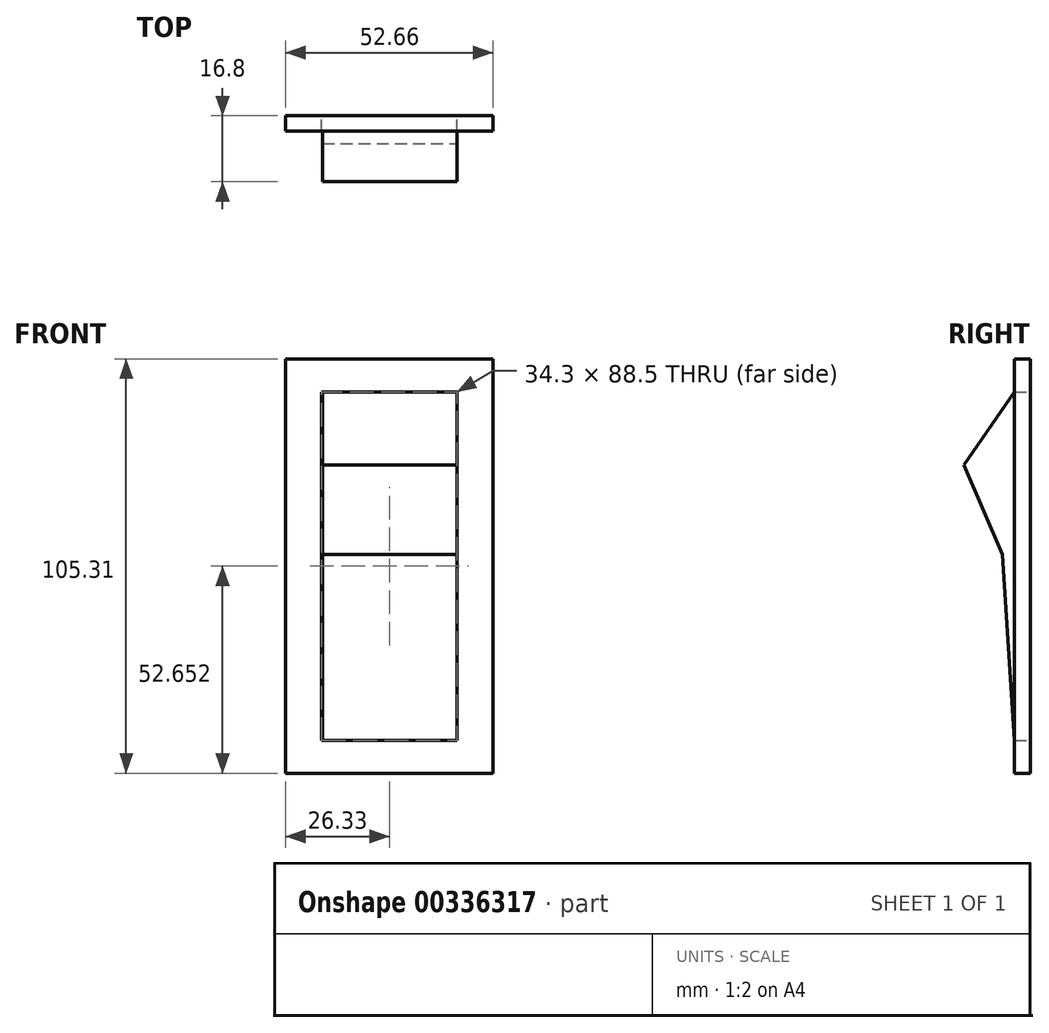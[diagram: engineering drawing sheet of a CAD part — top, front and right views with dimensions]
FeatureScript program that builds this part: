
annotation { "Feature Type Name" : "Feature", "Feature Type Description" : "" }
export const myFeature = defineFeature(function(context is Context, id is Id, definition is map)
    precondition{}
    {
        {
            var Q0;
            Q0=qCreatedBy(makeId("Front.planeOp"),FACE);
            var sketch = newSketch(context, id + "F0", { "sketchPlane" : qUnion([Q0])});
            skLineSegment(sketch, "E0.bottom", {"start": v(-29.07, 12.82) * mm, "end": v(-81.73, 12.82) * mm});
            skLineSegment(sketch, "E0.top", {"start": v(-29.07, 118.13) * mm, "end": v(-81.73, 118.13) * mm});
            skLineSegment(sketch, "E0.left", {"start": v(-29.07, 12.82) * mm, "end": v(-29.07, 118.13) * mm});
            skLineSegment(sketch, "E0.right", {"start": v(-81.73, 12.82) * mm, "end": v(-81.73, 118.13) * mm});
            skPoint(sketch, "E0.middle", {"position": v(-55.4, 65.47) * mm});
            skLineSegment(sketch, "E1.bottom", {"start": v(-72.55, 109.72) * mm, "end": v(-38.25, 109.72) * mm});
            skLineSegment(sketch, "E1.top", {"start": v(-72.55, 21.22) * mm, "end": v(-38.25, 21.22) * mm});
            skLineSegment(sketch, "E1.left", {"start": v(-72.55, 109.72) * mm, "end": v(-72.55, 21.22) * mm});
            skLineSegment(sketch, "E1.right", {"start": v(-38.25, 109.72) * mm, "end": v(-38.25, 21.22) * mm});
            skSolve(sketch);
        }
        {
            var Q0;
            Q0=makeQuery(id+"F0.imprint","IMPRINT",FACE,{"disambiguationData":[TD([[makeQuery(id+"F0.imprint","IMPRINT",EDGE,{"derivedFrom":sQuery(id+"F0.wireOp",EDGE,"E0.bottom")}),-1.0]])]});
            extrude(context, id + "F1", {"entities" : qUnion([Q0]), "depth" : 4 * mm});
        }
        {
            var Q0;
            Q0=makeQuery(id+"F1.opExtrude","SWEPT_FACE",FACE,{"disambiguationData":[OSD([sQuery(id+"F0.wireOp",EDGE,"E1.right")])]});
            var sketch = newSketch(context, id + "F2", { "sketchPlane" : qUnion([Q0])});
            skLineSegment(sketch, "E2", {"start": v(4, 109.72) * mm, "end": v(16.8, 91.12) * mm});
            skLineSegment(sketch, "E3", {"start": v(16.8, 91.12) * mm, "end": v(7.07, 68.43) * mm});
            skLineSegment(sketch, "E4", {"start": v(7.07, 68.43) * mm, "end": v(4, 21.22) * mm});
            skSolve(sketch);
        }
        {
            var Q0;
            Q0=makeQuery(id+"F2.imprint","IMPRINT",FACE,{"disambiguationData":[TD([[makeQuery(id+"F2.imprint","IMPRINT",EDGE,{"derivedFrom":sQuery(id+"F2.wireOp",EDGE,"E2")}),-1.0]])]});
            extrude(context, id + "F3", {"entities" : qUnion([Q0]), "depth" : 34.1 * mm});
        }
    });
